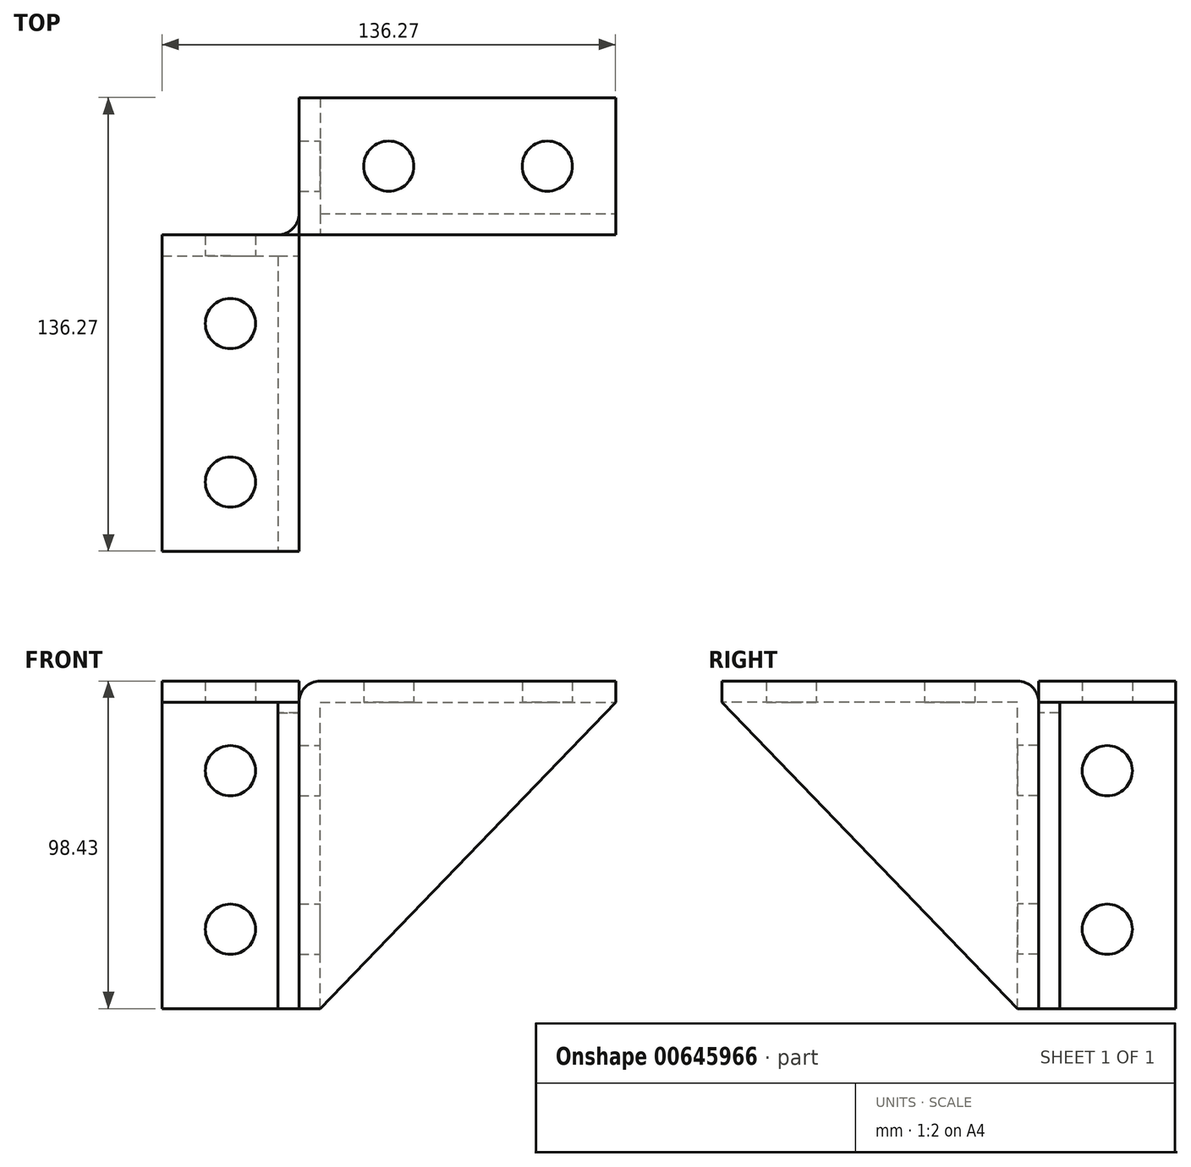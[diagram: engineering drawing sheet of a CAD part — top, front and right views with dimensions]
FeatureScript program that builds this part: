
annotation { "Feature Type Name" : "Feature", "Feature Type Description" : "" }
export const myFeature = defineFeature(function(context is Context, id is Id, definition is map)
    precondition{}
    {
        {
            var Q0;
            Q0=qCreatedBy(makeId("Right.planeOp"),FACE);
            var sketch = newSketch(context, id + "F0", { "sketchPlane" : qUnion([Q0])});
            skLineSegment(sketch, "E0", {"start": v(-95.07, 98.43) * mm, "end": v(0, 98.43) * mm});
            skLineSegment(sketch, "E1", {"start": v(0, 98.43) * mm, "end": v(0, 0) * mm});
            skLineSegment(sketch, "E2", {"start": v(0, 0) * mm, "end": v(-6.35, 0) * mm});
            skLineSegment(sketch, "E3", {"start": v(-6.35, 0) * mm, "end": v(-6.35, 92.08) * mm});
            skLineSegment(sketch, "E4", {"start": v(-6.35, 92.08) * mm, "end": v(-95.07, 92.08) * mm});
            skLineSegment(sketch, "E5", {"start": v(-95.07, 92.08) * mm, "end": v(-95.07, 98.43) * mm});
            skSolve(sketch);
        }
        {
            var Q0;
            Q0=makeQuery(id+"F0.imprint","IMPRINT",FACE,{"disambiguationData":[TD([[makeQuery(id+"F0.imprint","IMPRINT",EDGE,{"derivedFrom":sQuery(id+"F0.wireOp",EDGE,"E0")}),-1.0]])]});
            extrude(context, id + "F1", {"entities" : qUnion([Q0]), "oppositeDirection" : true, "depth" : 41.2 * mm, "offsetDistance" : 25.4 * mm});
        }
        {
            var Q0;
            Q0=qCreatedBy(makeId("Front.planeOp"),FACE);
            var sketch = newSketch(context, id + "F2", { "sketchPlane" : qUnion([Q0])});
            skLineSegment(sketch, "E6", {"start": v(95.07, 98.43) * mm, "end": v(0, 98.43) * mm});
            skLineSegment(sketch, "E7", {"start": v(0, 98.42) * mm, "end": v(0, 0) * mm});
            skLineSegment(sketch, "E8", {"start": v(0, 0) * mm, "end": v(6.35, 0) * mm});
            skLineSegment(sketch, "E9", {"start": v(6.35, 0) * mm, "end": v(6.35, 92.08) * mm});
            skLineSegment(sketch, "E10", {"start": v(6.35, 92.08) * mm, "end": v(95.07, 92.08) * mm});
            skLineSegment(sketch, "E11", {"start": v(95.07, 92.08) * mm, "end": v(95.07, 98.43) * mm});
            skSolve(sketch);
        }
        {
            var Q0;
            Q0=makeQuery(id+"F2.imprint","IMPRINT",FACE,{"disambiguationData":[TD([[makeQuery(id+"F2.imprint","IMPRINT",EDGE,{"derivedFrom":sQuery(id+"F2.wireOp",EDGE,"E6")}),1.0]])]});
            extrude(context, id + "F3", {"entities" : qUnion([Q0]), "operationType" : NewBodyOperationType.ADD, "oppositeDirection" : true, "depth" : 41.2 * mm, "offsetDistance" : 25.4 * mm});
        }
        {
            var Q0;
            Q0=makeQuery(id+"F1.opExtrude","SWEPT_EDGE",EDGE,{"disambiguationData":[OSD([sQuery(id+"F0.wireOp",EDGE,"E0"),sQuery(id+"F0.wireOp",EDGE,"E1")])]});
            fillet(context, id + "F4", {"entities" : qUnion([Q0]), "radius" : 6.35 * mm, "allowEdgeOverflow" : false});
        }
        {
            var Q0;
            Q0=makeQuery(id+"F3.opExtrude","SWEPT_EDGE",EDGE,{"disambiguationData":[OSD([sQuery(id+"F2.wireOp",EDGE,"E6"),sQuery(id+"F2.wireOp",EDGE,"E7")])]});
            fillet(context, id + "F5", {"entities" : qUnion([Q0]), "radius" : 6.35 * mm, "tangentPropagation" : true, "allowEdgeOverflow" : false});
        }
        {
            var Q0;
            Q0=makeQuery(id+"F1.opExtrude","SWEPT_FACE",FACE,{"disambiguationData":[OSD([sQuery(id+"F0.wireOp",EDGE,"E1")])]});
            cPlane(context, id + "F6", {"entities" : qUnion([Q0]), "cplaneType" : CPlaneType.OFFSET, "offset" : 0 * mm, "width" : 152.4 * mm, "height" : 152.4 * mm});
        }
        {
            var Q0;
            Q0=qCreatedBy(id+"F6.planeOp",FACE);
            var sketch = newSketch(context, id + "F7", { "sketchPlane" : qUnion([Q0])});
            skPoint(sketch, "E12", {"position": v(20.6, 23.84) * mm});
            skPoint(sketch, "E13", {"position": v(20.6, 71.47) * mm});
            skSolve(sketch);
        }
        {
            var Q0;
            Q0=makeQuery(id+"F1.opExtrude","SWEPT_FACE",FACE,{"disambiguationData":[OSD([sQuery(id+"F0.wireOp",EDGE,"E0")])]});
            cPlane(context, id + "F8", {"entities" : qUnion([Q0]), "cplaneType" : CPlaneType.OFFSET, "offset" : 0 * mm, "width" : 152.4 * mm, "height" : 152.4 * mm});
        }
        {
            var Q0;
            Q0=qCreatedBy(id+"F8.planeOp",FACE);
            var sketch = newSketch(context, id + "F9", { "sketchPlane" : qUnion([Q0])});
            skPoint(sketch, "E14", {"position": v(-20.6, -26.69) * mm});
            skPoint(sketch, "E15", {"position": v(-20.6, -74.31) * mm});
            skSolve(sketch);
        }
        {
            var Q0;
            Q0=makeQuery(id+"F3.opExtrude","SWEPT_FACE",FACE,{"disambiguationData":[OSD([sQuery(id+"F2.wireOp",EDGE,"E7")])]});
            cPlane(context, id + "F10", {"entities" : qUnion([Q0]), "cplaneType" : CPlaneType.OFFSET, "offset" : 0 * mm, "width" : 152.4 * mm, "height" : 152.4 * mm});
        }
        {
            var Q0;
            Q0=qCreatedBy(id+"F10.planeOp",FACE);
            var sketch = newSketch(context, id + "F11", { "sketchPlane" : qUnion([Q0])});
            skPoint(sketch, "E16", {"position": v(-20.6, 23.84) * mm});
            skPoint(sketch, "E17", {"position": v(-20.6, 71.47) * mm});
            skSolve(sketch);
        }
        {
            var Q0;
            Q0=makeQuery(id+"F3.opExtrude","SWEPT_FACE",FACE,{"disambiguationData":[OSD([sQuery(id+"F2.wireOp",EDGE,"E6")])]});
            cPlane(context, id + "F12", {"entities" : qUnion([Q0]), "cplaneType" : CPlaneType.OFFSET, "offset" : 0 * mm, "width" : 152.4 * mm, "height" : 152.4 * mm});
        }
        {
            var Q0;
            Q0=qCreatedBy(id+"F12.planeOp",FACE);
            var sketch = newSketch(context, id + "F13", { "sketchPlane" : qUnion([Q0])});
            skPoint(sketch, "E18", {"position": v(26.94, 20.6) * mm});
            skPoint(sketch, "E19", {"position": v(74.56, 20.6) * mm});
            skSolve(sketch);
        }
        {
            var Q0;
            Q0=sQuery(id+"F7.wireOp",VERTEX,"E12");
            var Q1;
            Q1=sQuery(id+"F7.wireOp",VERTEX,"E13");
            var Q2;
            Q2=sQuery(id+"F9.wireOp",VERTEX,"E14");
            var Q3;
            Q3=sQuery(id+"F9.wireOp",VERTEX,"E15");
            var Q4;
            Q4=sQuery(id+"F11.wireOp",VERTEX,"E16");
            var Q5;
            Q5=sQuery(id+"F11.wireOp",VERTEX,"E17");
            var Q6;
            Q6=sQuery(id+"F13.wireOp",VERTEX,"E18");
            var Q7;
            Q7=sQuery(id+"F13.wireOp",VERTEX,"E19");
            var Q8;
            Q8=makeQuery(id+"F1.opExtrude","SWEPT_BODY",BODY,{"disambiguationData":[OSD([sQuery(id+"F0.wireOp",EDGE,"E0"),sQuery(id+"F0.wireOp",EDGE,"E1"),sQuery(id+"F0.wireOp",EDGE,"E2"),sQuery(id+"F0.wireOp",EDGE,"E3"),sQuery(id+"F0.wireOp",EDGE,"E4"),sQuery(id+"F0.wireOp",EDGE,"E5")])]});
            var Q9;
            Q9=makeQuery(id+"F3.opExtrude","SWEPT_BODY",BODY,{"disambiguationData":[OSD([sQuery(id+"F2.wireOp",EDGE,"E6"),sQuery(id+"F2.wireOp",EDGE,"E7"),sQuery(id+"F2.wireOp",EDGE,"E8"),sQuery(id+"F2.wireOp",EDGE,"E9"),sQuery(id+"F2.wireOp",EDGE,"E10"),sQuery(id+"F2.wireOp",EDGE,"E11")])]});
            hole(context, id + "F14", {"style" : HoleStyle.SIMPLE, "endStyle" : HoleEndStyle.THROUGH, "standardTappedOrClearance" : lookupTablePath({ "fit" : "Free", "standard" : "ANSI", "size" : "9/16", "type" : "Clearance" }), "standardBlindInLast" : lookupTablePath({ "fit" : "Normal", "standard" : "ANSI", "engagement" : "75%", "pitch" : "12 tpi", "size" : "9/16", "type" : "Clearance & tapped" }), "holeDiameter" : 15.08 * mm, "majorDiameter" : 6.35 * mm, "tappedDepth" : 12.7 * mm, "tapClearance" : 3, "locations" : qUnion([Q0, Q1, Q2, Q3, Q4, Q5, Q6, Q7]), "scope" : qUnion([Q8, Q9]), "startStyle" : HoleStartStyle.PART});
        }
        {
            var Q0;
            Q0=makeQuery(id+"F1.opExtrude","SWEPT_FACE",FACE,{"disambiguationData":[OSD([sQuery(id+"F0.wireOp",EDGE,"E2")])]});
            cPlane(context, id + "F15", {"entities" : qUnion([Q0]), "cplaneType" : CPlaneType.OFFSET, "offset" : 0 * mm, "width" : 152.4 * mm, "height" : 152.4 * mm});
        }
        {
            var Q0;
            Q0=qCreatedBy(id+"F15.planeOp",FACE);
            var sketch = newSketch(context, id + "F16", { "sketchPlane" : qUnion([Q0])});
            skPoint(sketch, "E20.visualSharp", {"position": v(0, 0) * mm});
            skArc(sketch, "E21.filletArc", {"start": v(0, -6.35) * mm, "mid": v(-1.86, -1.86) * mm, "end": v(-6.35, 0) * mm});
            skLineSegment(sketch, "E22", {"start": v(-6.35, 0) * mm, "end": v(0, 0) * mm});
            skLineSegment(sketch, "E23", {"start": v(0, -6.35) * mm, "end": v(0, 0) * mm});
            skSolve(sketch);
        }
        {
            var Q0;
            Q0=makeQuery(id+"F16.imprint","IMPRINT",FACE,{"disambiguationData":[TD([[makeQuery(id+"F16.imprint","IMPRINT",EDGE,{"derivedFrom":sQuery(id+"F16.wireOp",EDGE,"E21.filletArc")}),-1.0]])]});
            extrude(context, id + "F17", {"entities" : qUnion([Q0]), "oppositeDirection" : true, "depth" : 88.9 * mm, "offsetDistance" : 25.4 * mm});
        }
        {
            var Q0;
            Q0=makeQuery(id+"F1.opExtrude","CAP_FACE",FACE,{"disambiguationData":[OSD([sQuery(id+"F0.wireOp",EDGE,"E0"),sQuery(id+"F0.wireOp",EDGE,"E1"),sQuery(id+"F0.wireOp",EDGE,"E2"),sQuery(id+"F0.wireOp",EDGE,"E3"),sQuery(id+"F0.wireOp",EDGE,"E4"),sQuery(id+"F0.wireOp",EDGE,"E5")])],"isStart":true});
            cPlane(context, id + "F18", {"entities" : qUnion([Q0]), "cplaneType" : CPlaneType.OFFSET, "offset" : 0 * mm, "width" : 152.4 * mm, "height" : 152.4 * mm});
        }
        {
            var Q0;
            Q0=qCreatedBy(id+"F18.planeOp",FACE);
            var sketch = newSketch(context, id + "F19", { "sketchPlane" : qUnion([Q0])});
            skLineSegment(sketch, "E24.0", {"start": v(-6.35, 92.08) * mm, "end": v(-95.07, 92.08) * mm});
            skLineSegment(sketch, "E25.0", {"start": v(-6.35, 0) * mm, "end": v(-6.35, 92.08) * mm});
            skLineSegment(sketch, "E26", {"start": v(-95.07, 92.07) * mm, "end": v(-6.35, 0) * mm});
            skSolve(sketch);
        }
        {
            var Q0;
            Q0=makeQuery(id+"F19.imprint","IMPRINT",FACE,{"disambiguationData":[TD([[makeQuery(id+"F19.imprint","IMPRINT",EDGE,{"derivedFrom":sQuery(id+"F19.wireOp",EDGE,"E24.0")}),1.0]])]});
            extrude(context, id + "F20", {"entities" : qUnion([Q0]), "operationType" : NewBodyOperationType.ADD, "oppositeDirection" : true, "depth" : 6.35 * mm, "offsetDistance" : 25.4 * mm});
        }
        {
            var Q0;
            Q0=makeQuery(id+"F3.opExtrude","CAP_FACE",FACE,{"disambiguationData":[OSD([sQuery(id+"F2.wireOp",EDGE,"E6"),sQuery(id+"F2.wireOp",EDGE,"E7"),sQuery(id+"F2.wireOp",EDGE,"E8"),sQuery(id+"F2.wireOp",EDGE,"E9"),sQuery(id+"F2.wireOp",EDGE,"E10"),sQuery(id+"F2.wireOp",EDGE,"E11")])],"isStart":true});
            cPlane(context, id + "F21", {"entities" : qUnion([Q0]), "cplaneType" : CPlaneType.OFFSET, "offset" : 0 * mm, "width" : 152.4 * mm, "height" : 152.4 * mm});
        }
        {
            var Q0;
            Q0=qCreatedBy(id+"F21.planeOp",FACE);
            var sketch = newSketch(context, id + "F22", { "sketchPlane" : qUnion([Q0])});
            skLineSegment(sketch, "E27.0", {"start": v(6.35, 92.08) * mm, "end": v(95.07, 92.08) * mm});
            skLineSegment(sketch, "E28.0", {"start": v(6.35, 0) * mm, "end": v(6.35, 92.08) * mm});
            skLineSegment(sketch, "E29", {"start": v(6.35, 0) * mm, "end": v(95.07, 92.07) * mm});
            skSolve(sketch);
        }
        {
            var Q0;
            Q0=makeQuery(id+"F22.imprint","IMPRINT",FACE,{"disambiguationData":[TD([[makeQuery(id+"F22.imprint","IMPRINT",EDGE,{"derivedFrom":sQuery(id+"F22.wireOp",EDGE,"E27.0")}),-1.0]])]});
            extrude(context, id + "F23", {"entities" : qUnion([Q0]), "operationType" : NewBodyOperationType.ADD, "oppositeDirection" : true, "depth" : 6.35 * mm, "offsetDistance" : 25.4 * mm});
        }
    });
